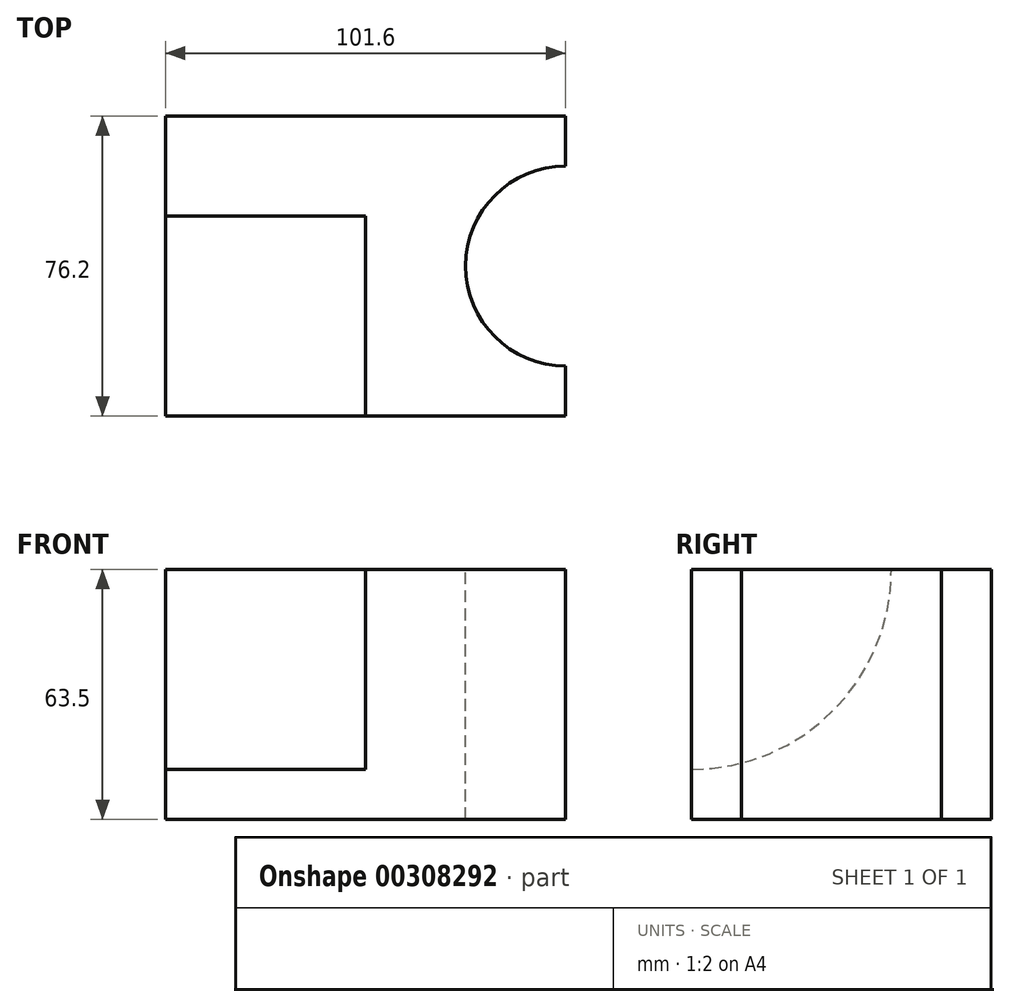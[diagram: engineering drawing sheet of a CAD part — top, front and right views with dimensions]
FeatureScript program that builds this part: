
annotation { "Feature Type Name" : "Feature", "Feature Type Description" : "" }
export const myFeature = defineFeature(function(context is Context, id is Id, definition is map)
    precondition{}
    {
        {
            var Q0;
            Q0=qCreatedBy(makeId("Front.planeOp"),FACE);
            var sketch = newSketch(context, id + "F0", { "sketchPlane" : qUnion([Q0])});
            skLineSegment(sketch, "E0", {"start": v(-51.28, -48.54) * mm, "end": v(50.32, -48.54) * mm});
            skLineSegment(sketch, "E1", {"start": v(50.32, -48.54) * mm, "end": v(50.32, 14.96) * mm});
            skLineSegment(sketch, "E2", {"start": v(50.32, 14.96) * mm, "end": v(-51.28, 14.96) * mm});
            skLineSegment(sketch, "E3", {"start": v(-51.28, 14.96) * mm, "end": v(-51.28, -48.54) * mm});
            skSolve(sketch);
        }
        {
            var Q0;
            Q0=makeQuery(id+"F0.imprint","IMPRINT",FACE,{"disambiguationData":[TD([[makeQuery(id+"F0.imprint","IMPRINT",EDGE,{"derivedFrom":sQuery(id+"F0.wireOp",EDGE,"E0")}),1.0]])]});
            extrude(context, id + "F1", {"entities" : qUnion([Q0]), "depth" : 76.2 * mm});
        }
        {
            var Q0;
            Q0=makeQuery(id+"F1.opExtrude","SWEPT_FACE",FACE,{"disambiguationData":[OSD([sQuery(id+"F0.wireOp",EDGE,"E2")])]});
            var sketch = newSketch(context, id + "F2", { "sketchPlane" : qUnion([Q0])});
            skArc(sketch, "E4", {"start": v(50.32, -12.7) * mm, "mid": v(24.92, -38.1) * mm, "end": v(50.32, -63.5) * mm});
            skLineSegment(sketch, "E5", {"start": v(50.32, -76.2) * mm, "end": v(50.32, 0) * mm});
            skSolve(sketch);
        }
        {
            var Q0;
            {var subQ0=sQuery(id+"F2.wireOp",EDGE,"E4");Q0=makeQuery(id+"F2.imprint","IMPRINT",FACE,{"disambiguationData":[TD([[makeQuery(id+"F2.imprint","IMPRINT",EDGE,{"derivedFrom":subQ0}),1.0]])]});}
            extrude(context, id + "F3", {"entities" : qUnion([Q0]), "operationType" : NewBodyOperationType.REMOVE, "oppositeDirection" : true, "depth" : 63.5 * mm});
        }
        {
            var Q0;
            Q0=makeQuery(id+"F1.opExtrude","SWEPT_FACE",FACE,{"disambiguationData":[OSD([sQuery(id+"F0.wireOp",EDGE,"E3")])]});
            var sketch = newSketch(context, id + "F4", { "sketchPlane" : qUnion([Q0])});
            skArc(sketch, "E6", {"start": v(25.4, 14.96) * mm, "mid": v(40.28, -20.96) * mm, "end": v(76.2, -35.84) * mm});
            skLineSegment(sketch, "E7", {"start": v(0, 14.96) * mm, "end": v(76.2, 14.96) * mm});
            skLineSegment(sketch, "E8", {"start": v(76.2, 14.96) * mm, "end": v(76.2, -48.54) * mm});
            skSolve(sketch);
        }
        {
            var Q0;
            {var subQ0=sQuery(id+"F4.wireOp",EDGE,"E6");Q0=makeQuery(id+"F4.imprint","IMPRINT",FACE,{"disambiguationData":[TD([[makeQuery(id+"F4.imprint","IMPRINT",EDGE,{"derivedFrom":subQ0}),1.0]])]});}
            extrude(context, id + "F5", {"entities" : qUnion([Q0]), "operationType" : NewBodyOperationType.REMOVE, "oppositeDirection" : true, "depth" : 50.8 * mm});
        }
    });
